# Revit family: Скамейка стальная «Авиньон» Арт 15496
name_source: partatom
category: Антураж
revit_build: Autodesk Revit 2018 (Build: 20180423_1000(x64)
units: mm (PartAtom-declared; Revit-internal decimal feet)

## family parameters
Всегда вертикально = Да
Источник визуального образа = Геометрия семейства
На основе рабочей плоскости = Нет
Общий = Нет
При загрузке вырезать с полостями = Нет
Точка расчета площади = Нет

## types (2) — shared parameters
URL = https://hobbyka.ru
Артикул товара = Арт. 15496
Высота = 1000 мм
Группа модели = Скамейки
Длина = 2250 мм
Изготовитель = ООО «Хоббика»
Изображение типоразмера = Скамейка стальная «Авиньон» Арт 15496.jpg
Материал изделия = Сталь, дерево
Цвет опоры = Сталь
Ширина = 740 мм

## per-type parameters (varying)
| type | Версия 2,25 м (лиственница) | Версия 2,25 м (сосна) | Описание | Цвет лавки |
| Версия 2,25 м (лиственница) | Да | Нет | Скамейка стальная «Авиньон». Версия 2,25 м (лиственница) | Лиственница |
| Версия 2,25 м (сосна) | Нет | Да | Скамейка стальная «Авиньон». Версия 2,25 м (сосна) | Сосна |
